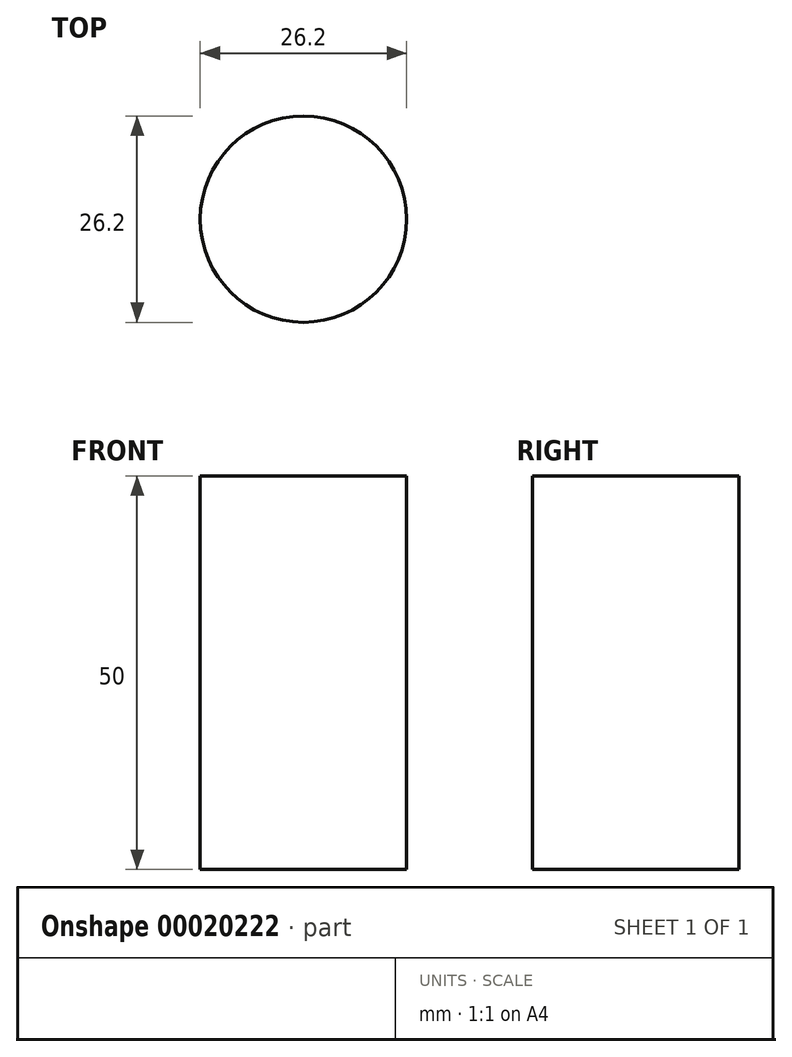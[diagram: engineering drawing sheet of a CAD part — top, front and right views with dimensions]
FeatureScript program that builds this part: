
annotation { "Feature Type Name" : "Feature", "Feature Type Description" : "" }
export const myFeature = defineFeature(function(context is Context, id is Id, definition is map)
    precondition{}
    {
        {
            var Q0;
            Q0=qCreatedBy(makeId("Top.planeOp"),FACE);
            var sketch = newSketch(context, id + "F0", { "sketchPlane" : qUnion([Q0])});
            skCircle(sketch, "E0", {"center": v(0, 0) * mm, "radius": 13.1 * mm});
            skSolve(sketch);
        }
        {
            var Q0;
            Q0=makeQuery(id+"F0.imprint","IMPRINT",FACE,{"disambiguationData":[TD([[makeQuery(id+"F0.imprint","IMPRINT",EDGE,{"derivedFrom":sQuery(id+"F0.wireOp",EDGE,"E0")}),1.0]])]});
            var Q1;
            Q1=sQuery(id+"F0.wireOp",EDGE,"E0");
            extrude(context, id + "F1", {"entities" : qUnion([Q0]), "surfaceEntities" : qUnion([Q1]), "depth" : 50 * mm});
        }
    });
